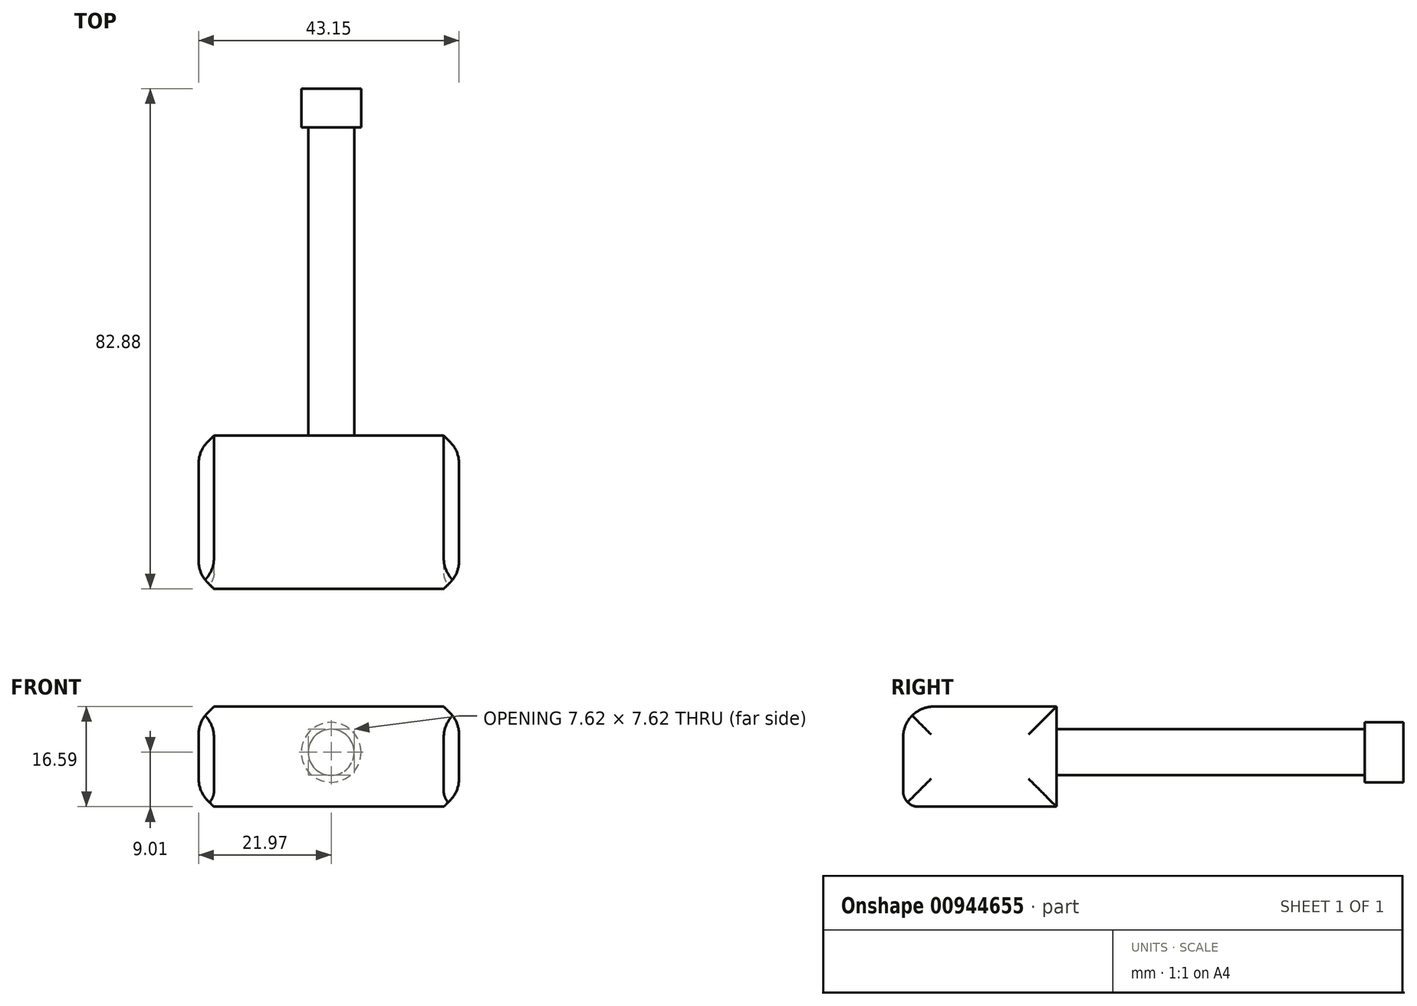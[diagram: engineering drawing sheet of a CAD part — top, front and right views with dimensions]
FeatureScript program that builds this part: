
annotation { "Feature Type Name" : "Feature", "Feature Type Description" : "" }
export const myFeature = defineFeature(function(context is Context, id is Id, definition is map)
    precondition{}
    {
        {
            var Q0;
            Q0=qCreatedBy(makeId("Front.planeOp"),FACE);
            var sketch = newSketch(context, id + "F0", { "sketchPlane" : qUnion([Q0])});
            skCircle(sketch, "E0", {"center": v(0, 0) * mm, "radius": 3.8 * mm});
            skSolve(sketch);
        }
        {
            var Q0;
            Q0=makeQuery(id+"F0.imprint","IMPRINT",FACE,{"disambiguationData":[TD([[makeQuery(id+"F0.imprint","IMPRINT",EDGE,{"derivedFrom":sQuery(id+"F0.wireOp",EDGE,"E0")}),1.0]])]});
            extrude(context, id + "F1", {"entities" : qUnion([Q0]), "depth" : 51.05 * mm, "offsetDistance" : 25.4 * mm});
        }
        {
            var Q0;
            Q0=makeQuery(id+"F1.opExtrude","CAP_FACE",FACE,{"disambiguationData":[OSD([sQuery(id+"F0.wireOp",EDGE,"E0")])],"isStart":false});
            var sketch = newSketch(context, id + "F2", { "sketchPlane" : qUnion([Q0])});
            skLineSegment(sketch, "E1.bottom", {"start": v(-21.97, -9.01) * mm, "end": v(21.18, -9.01) * mm});
            skLineSegment(sketch, "E1.top", {"start": v(-21.97, 7.58) * mm, "end": v(21.18, 7.58) * mm});
            skLineSegment(sketch, "E1.left", {"start": v(-21.97, -9.01) * mm, "end": v(-21.97, 7.58) * mm});
            skLineSegment(sketch, "E1.right", {"start": v(21.18, -9.01) * mm, "end": v(21.18, 7.58) * mm});
            skSolve(sketch);
        }
        {
            var Q0;
            Q0=makeQuery(id+"F2.imprint","IMPRINT",FACE,{"disambiguationData":[TD([[makeQuery(id+"F2.imprint","IMPRINT",EDGE,{"derivedFrom":sQuery(id+"F2.wireOp",EDGE,"E1.bottom")}),1.0]])]});
            var Q1;
            Q1=makeQuery(id+"F2.imprint","IMPRINT",FACE,{"disambiguationData":[TD([[makeQuery(id+"F2.imprint","IMPRINT",EDGE,{"derivedFrom":makeQuery(id+"F1.opExtrude","CAP_EDGE",EDGE,{"disambiguationData":[OSD([sQuery(id+"F0.wireOp",EDGE,"E0")])],"isStart":false})}),1.0]])]});
            extrude(context, id + "F3", {"entities" : qUnion([Q0, Q1]), "operationType" : NewBodyOperationType.ADD, "depth" : 25.4 * mm, "offsetDistance" : 25.4 * mm});
        }
        {
            var Q0;
            Q0=makeQuery(id+"F3.opExtrude","SWEPT_FACE",FACE,{"disambiguationData":[OSD([sQuery(id+"F2.wireOp",EDGE,"E1.right")])]});
            chamfer(context, id + "F4", {"entities" : qUnion([Q0]), "width" : 2.54 * mm, "tangentPropagation" : true});
        }
        {
            var Q0;
            Q0=makeQuery(id+"F3.opExtrude","SWEPT_FACE",FACE,{"disambiguationData":[OSD([sQuery(id+"F2.wireOp",EDGE,"E1.left")])]});
            chamfer(context, id + "F5", {"entities" : qUnion([Q0]), "width" : 2.54 * mm, "tangentPropagation" : true});
        }
        {
            var Q0;
            Q0=makeQuery(id+"F1.opExtrude","CAP_FACE",FACE,{"disambiguationData":[OSD([sQuery(id+"F0.wireOp",EDGE,"E0")])],"isStart":true});
            var sketch = newSketch(context, id + "F6", { "sketchPlane" : qUnion([Q0])});
            skCircle(sketch, "E2", {"center": v(0, 0) * mm, "radius": 4.95 * mm});
            skSolve(sketch);
        }
        {
            var Q0;
            Q0=makeQuery(id+"F6.imprint","IMPRINT",FACE,{"disambiguationData":[TD([[makeQuery(id+"F6.imprint","IMPRINT",EDGE,{"derivedFrom":makeQuery(id+"F1.opExtrude","CAP_EDGE",EDGE,{"disambiguationData":[OSD([sQuery(id+"F0.wireOp",EDGE,"E0")])],"isStart":true})}),-1.0]])]});
            extrude(context, id + "F7", {"entities" : qUnion([Q0]), "operationType" : NewBodyOperationType.ADD, "depth" : 6.43 * mm, "offsetDistance" : 25.4 * mm});
        }
        {
            var Q0;
            Q0=makeQuery(id+"F6.imprint","IMPRINT",FACE,{"disambiguationData":[TD([[makeQuery(id+"F6.imprint","IMPRINT",EDGE,{"derivedFrom":sQuery(id+"F6.wireOp",EDGE,"E2")}),1.0]])]});
            extrude(context, id + "F8", {"entities" : qUnion([Q0]), "operationType" : NewBodyOperationType.ADD, "depth" : 6.43 * mm, "offsetDistance" : 25.4 * mm});
        }
        {
            var Q0;
            Q0=makeQuery(id+"F3.opExtrude","CAP_EDGE",EDGE,{"disambiguationData":[OSD([sQuery(id+"F2.wireOp",EDGE,"E1.bottom")])],"isStart":false});
            fillet(context, id + "F9", {"entities" : qUnion([Q0]), "radius" : 2.54 * mm, "tangentPropagation" : true, "allowEdgeOverflow" : false});
        }
        {
            var Q0;
            Q0=makeQuery(id+"F3.opExtrude","CAP_EDGE",EDGE,{"disambiguationData":[OSD([sQuery(id+"F2.wireOp",EDGE,"E1.top")])],"isStart":false});
            var Q1;
            Q1=makeQuery(id+"F3.opExtrude","SWEPT_FACE",FACE,{"disambiguationData":[OSD([sQuery(id+"F2.wireOp",EDGE,"E1.left")])]});
            var Q2;
            Q2=makeQuery(id+"F3.opExtrude","SWEPT_FACE",FACE,{"disambiguationData":[OSD([sQuery(id+"F2.wireOp",EDGE,"E1.right")])]});
            fillet(context, id + "F10", {"entities" : qUnion([Q0, Q1, Q2]), "radius" : 5.08 * mm, "tangentPropagation" : true, "allowEdgeOverflow" : false});
        }
    });
